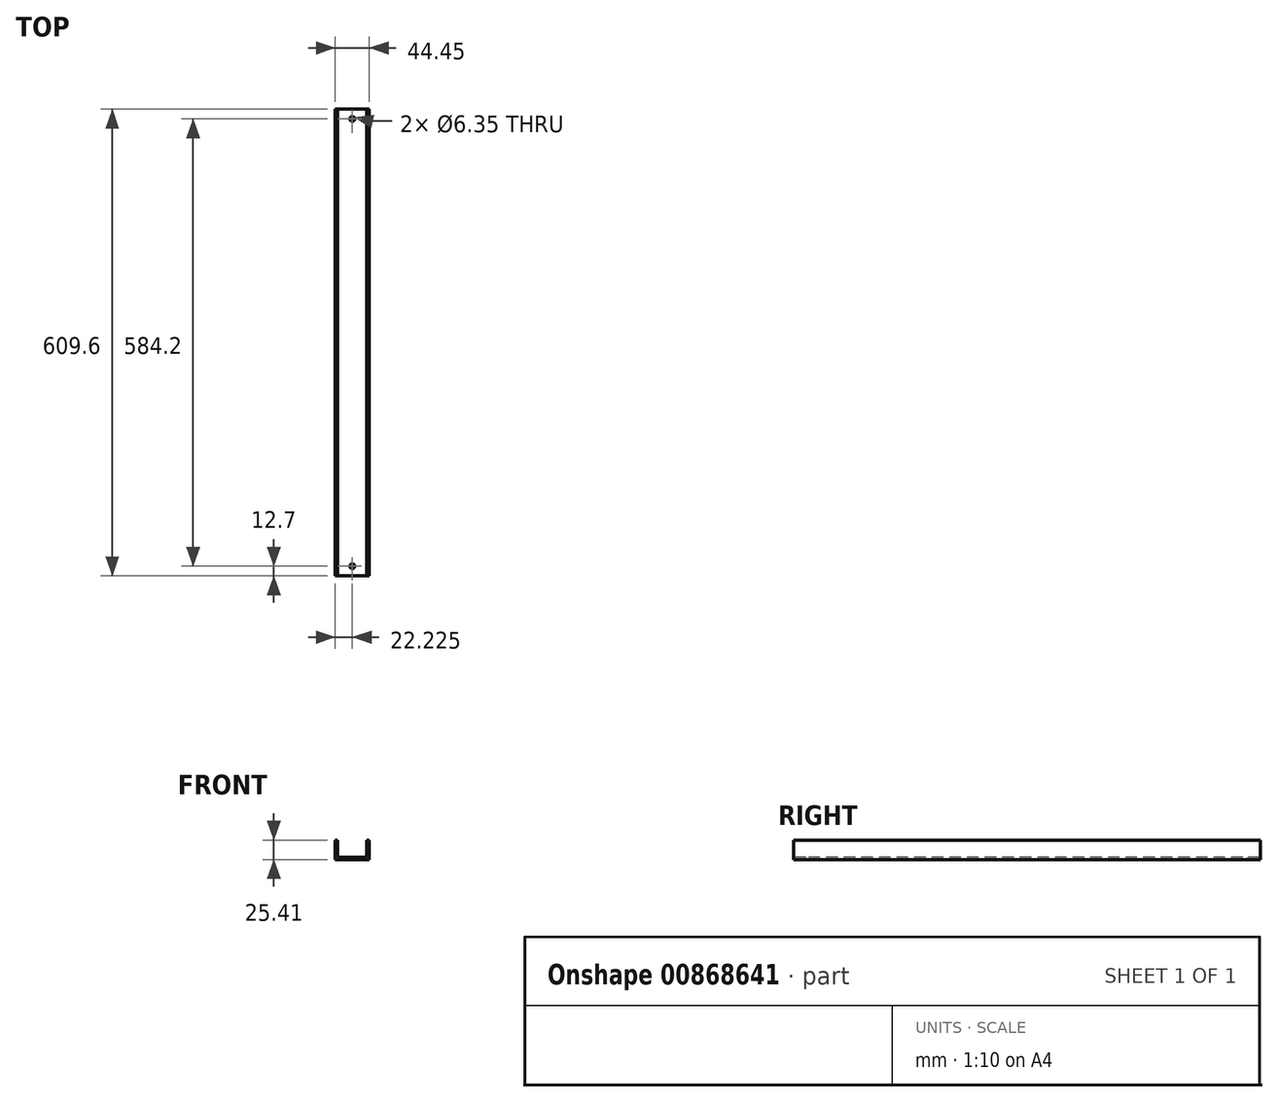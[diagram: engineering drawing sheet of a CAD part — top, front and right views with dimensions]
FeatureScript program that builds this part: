
annotation { "Feature Type Name" : "Feature", "Feature Type Description" : "" }
export const myFeature = defineFeature(function(context is Context, id is Id, definition is map)
    precondition{}
    {
        {
            var Q0;
            Q0=qCreatedBy(makeId("Top.planeOp"),FACE);
            var sketch = newSketch(context, id + "F0", { "sketchPlane" : qUnion([Q0])});
            skLineSegment(sketch, "E0.bottom", {"start": v(0, 0) * mm, "end": v(44.45, 0) * mm});
            skLineSegment(sketch, "E0.top", {"start": v(0, -609.6) * mm, "end": v(44.45, -609.6) * mm});
            skLineSegment(sketch, "E0.left", {"start": v(0, 0) * mm, "end": v(0, -609.6) * mm});
            skLineSegment(sketch, "E0.right", {"start": v(44.45, 0) * mm, "end": v(44.45, -609.6) * mm});
            skLineSegment(sketch, "E1", {"start": v(3.17, 0) * mm, "end": v(3.18, -609.6) * mm});
            skLineSegment(sketch, "E2", {"start": v(41.28, 0) * mm, "end": v(41.28, -609.6) * mm});
            skCircle(sketch, "E3", {"center": v(22.23, -12.7) * mm, "radius": 3.18 * mm});
            skCircle(sketch, "E4", {"center": v(22.23, -596.9) * mm, "radius": 3.18 * mm});
            skLineSegment(sketch, "E5", {"start": v(22.22, -609.6) * mm, "end": v(22.22, 0) * mm, "construction": true});
            skSolve(sketch);
        }
        {
            var Q0;
            Q0 = qSketchRegion(id + "F0", true);
            extrude(context, id + "F1", {"entities" : qUnion([Q0]), "oppositeDirection" : true, "depth" : 3.17 * mm, "offsetDistance" : 25.4 * mm});
        }
        {
            var Q0;
            {var subQ0=sQuery(id+"F0.wireOp",EDGE,"E0.left");Q0=makeQuery(id+"F0.imprint","IMPRINT",FACE,{"disambiguationData":[TD([[makeQuery(id+"F0.imprint","IMPRINT",EDGE,{"derivedFrom":subQ0}),1.0]])]});}
            var Q1;
            {var subQ0=sQuery(id+"F0.wireOp",EDGE,"E0.right");Q1=makeQuery(id+"F0.imprint","IMPRINT",FACE,{"disambiguationData":[TD([[makeQuery(id+"F0.imprint","IMPRINT",EDGE,{"derivedFrom":subQ0}),-1.0]])]});}
            extrude(context, id + "F2", {"entities" : qUnion([Q0, Q1]), "operationType" : NewBodyOperationType.ADD, "depth" : 22.22 * mm, "offsetDistance" : 25.4 * mm});
        }
    });
